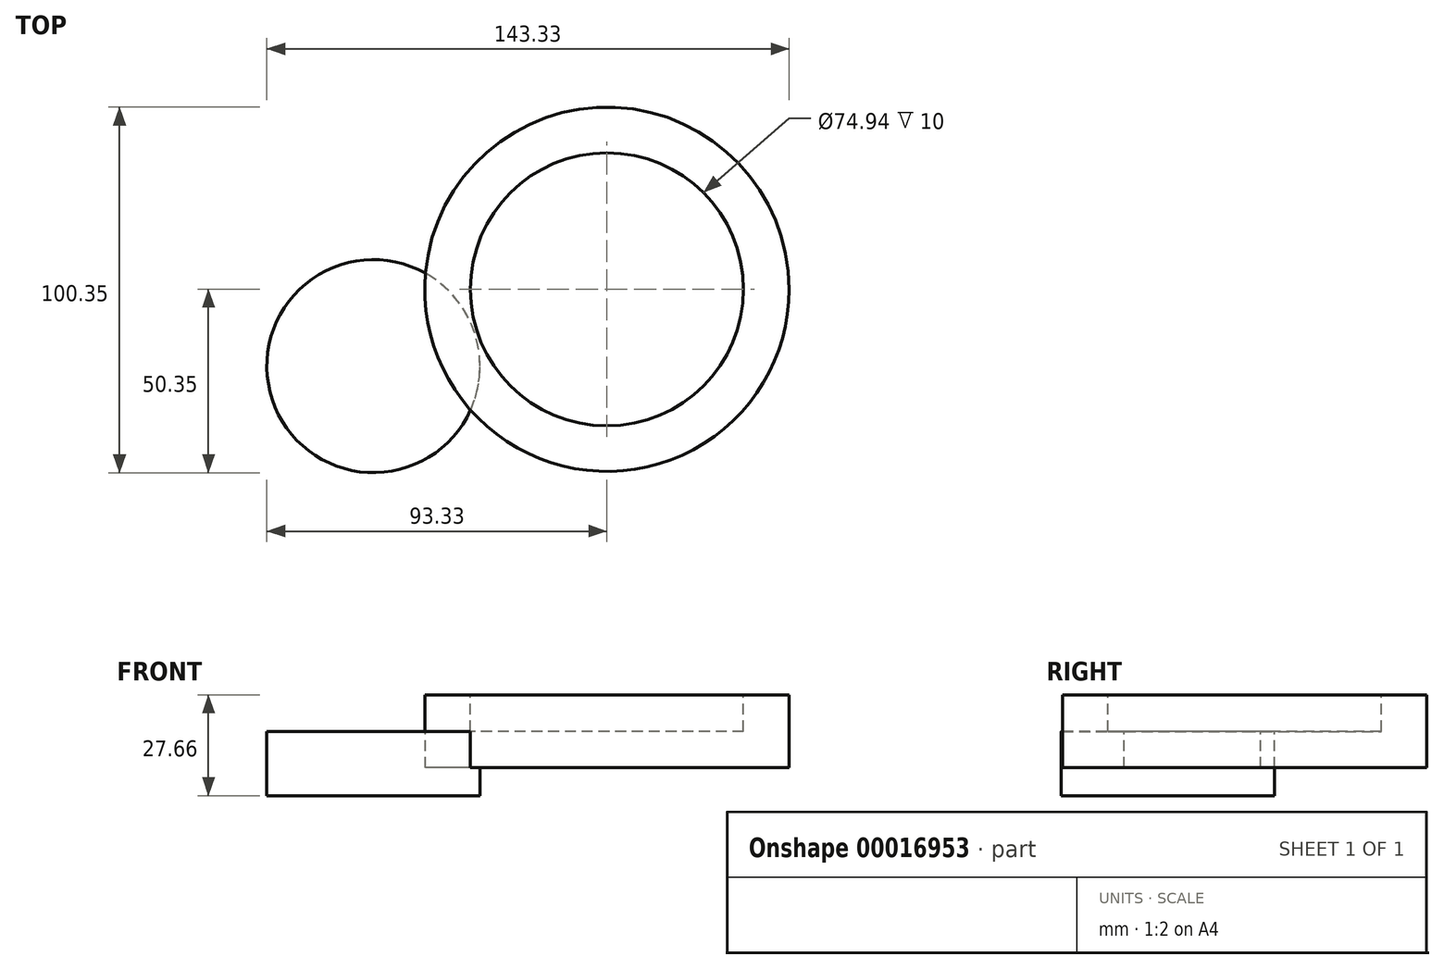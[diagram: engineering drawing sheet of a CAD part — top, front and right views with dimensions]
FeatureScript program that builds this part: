
annotation { "Feature Type Name" : "Feature", "Feature Type Description" : "" }
export const myFeature = defineFeature(function(context is Context, id is Id, definition is map)
    precondition{}
    {
        {
            var Q0;
            Q0=qCreatedBy(makeId("Top.planeOp"),FACE);
            var sketch = newSketch(context, id + "F0", { "sketchPlane" : qUnion([Q0])});
            skCircle(sketch, "E0", {"center": v(0, 0) * mm, "radius": 50 * mm});
            skSolve(sketch);
        }
        {
            var Q0;
            Q0=makeQuery(id+"F0.imprint","IMPRINT",FACE,{"disambiguationData":[TD([[makeQuery(id+"F0.imprint","IMPRINT",EDGE,{"derivedFrom":sQuery(id+"F0.wireOp",EDGE,"E0")}),1.0]])]});
            extrude(context, id + "F1", {"entities" : qUnion([Q0]), "depth" : 20 * mm});
        }
        {
            var Q0;
            Q0=makeQuery(id+"F1.opExtrude","CAP_FACE",FACE,{"disambiguationData":[OSD([sQuery(id+"F0.wireOp",EDGE,"E0")])],"isStart":false});
            var sketch = newSketch(context, id + "F2", { "sketchPlane" : qUnion([Q0])});
            skCircle(sketch, "E1", {"center": v(0, 0) * mm, "radius": 37.47 * mm});
            skSolve(sketch);
        }
        {
            var Q0;
            Q0=makeQuery(id+"F2.imprint","IMPRINT",FACE,{"disambiguationData":[TD([[makeQuery(id+"F2.imprint","IMPRINT",EDGE,{"derivedFrom":sQuery(id+"F2.wireOp",EDGE,"E1")}),1.0]])]});
            extrude(context, id + "F3", {"entities" : qUnion([Q0]), "operationType" : NewBodyOperationType.REMOVE, "oppositeDirection" : true, "depth" : 10 * mm});
        }
        {
            var Q0;
            Q0=makeQuery(id+"F3.boolean.opBoolean","COPY",FACE,{"derivedFrom":makeQuery(id+"F3.opExtrude","CAP_FACE",FACE,{"disambiguationData":[OSD([sQuery(id+"F2.wireOp",EDGE,"E1")])],"isStart":false})});
            var sketch = newSketch(context, id + "F4", { "sketchPlane" : qUnion([Q0])});
            skCircle(sketch, "E2", {"center": v(-64.1, -21.1) * mm, "radius": 29.24 * mm});
            skSolve(sketch);
        }
        {
            var Q0;
            Q0 = qSketchRegion(id + "F4", true);
            extrude(context, id + "F5", {"entities" : qUnion([Q0]), "operationType" : NewBodyOperationType.ADD, "oppositeDirection" : true, "depth" : 17.66 * mm});
        }
    });
